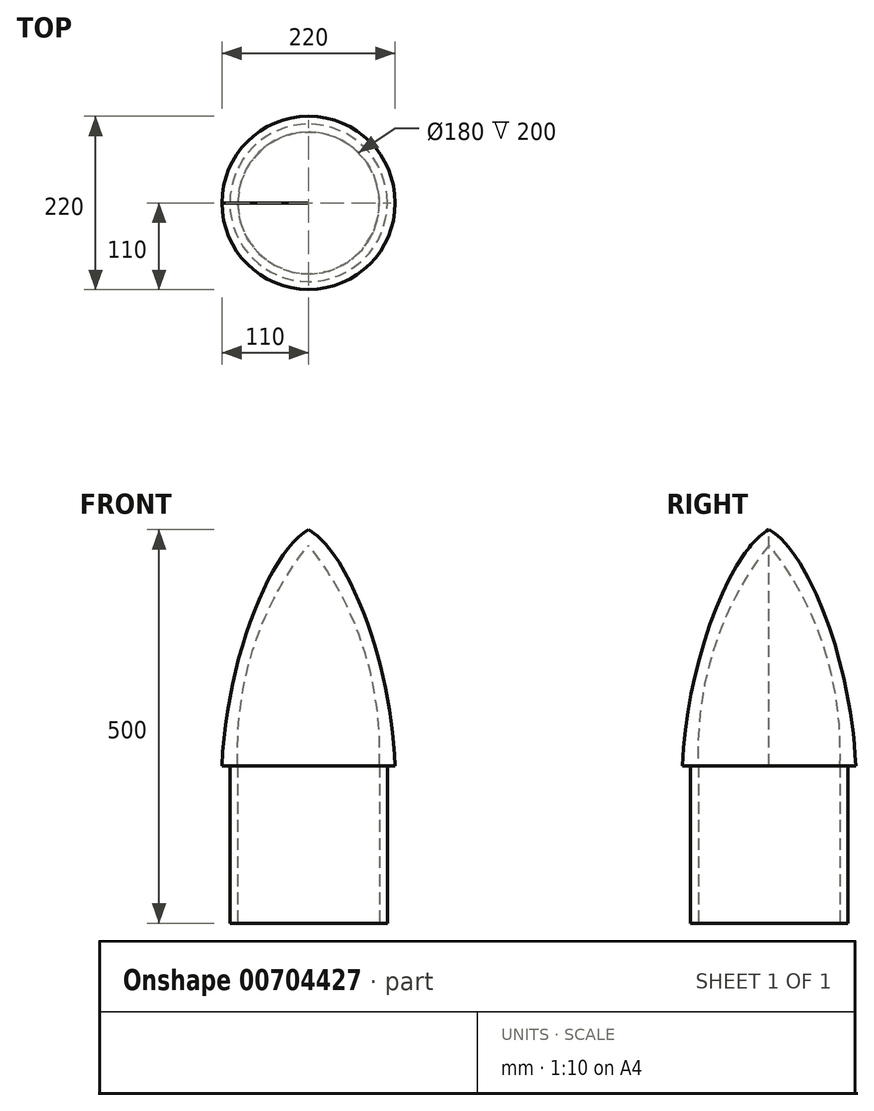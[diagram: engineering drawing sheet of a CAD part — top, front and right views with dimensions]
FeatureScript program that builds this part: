
annotation { "Feature Type Name" : "Feature", "Feature Type Description" : "" }
export const myFeature = defineFeature(function(context is Context, id is Id, definition is map)
    precondition{}
    {
        {
            var Q0;
            Q0=qCreatedBy(makeId("Front.planeOp"),FACE);
            var sketch = newSketch(context, id + "F0", { "sketchPlane" : qUnion([Q0])});
            skLineSegment(sketch, "E0", {"start": v(-100, -173.77) * mm, "end": v(-100, 26.23) * mm});
            skLineSegment(sketch, "E1", {"start": v(-100, 26.23) * mm, "end": v(-110, 26.23) * mm});
            skLineSegment(sketch, "E2", {"start": v(-100, -173.77) * mm, "end": v(-90, -173.77) * mm});
            skPoint(sketch, "E3.end.orphan", {"position": v(-90, 326.23) * mm});
            skLineSegment(sketch, "E4", {"start": v(-90, -173.77) * mm, "end": v(-90, 26.23) * mm});
            skFitSpline(sketch, "E5", {"points": [v(-110, 26.23) * mm, v(0, 326.23) * mm], "startDerivative": vector(16.28, 397.7) * mm, "endDerivative": vector(148.76, 81.36) * mm});
            skFitSpline(sketch, "E6", {"points": [v(-90, 26.23) * mm, v(0.03, 306.23) * mm], "startDerivative": vector(-19.06, 488.89) * mm, "endDerivative": vector(39.52, 47.98) * mm});
            skPoint(sketch, "E7.start.orphan", {"position": v(0, -184.53) * mm});
            skLineSegment(sketch, "E8", {"start": v(0, -184.53) * mm, "end": v(0, 362.03) * mm});
            skSolve(sketch);
        }
        {
            var Q0;
            Q0=makeQuery(id+"F0.imprint","IMPRINT",FACE,{"disambiguationData":[TD([[makeQuery(id+"F0.imprint","IMPRINT",EDGE,{"derivedFrom":sQuery(id+"F0.wireOp",EDGE,"E0")}),-1.0]])]});
            var Q1;
            Q1=sQuery(id+"F0.wireOp",EDGE,"E8");
            revolve(context, id + "F1", {"surfaceOperationType" : NewSurfaceOperationType.NEW, "entities" : qUnion([Q0]), "axis" : qUnion([Q1]), "revolveType" : RevolveType.FULL});
        }
    });
